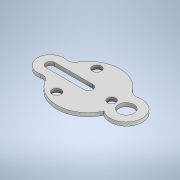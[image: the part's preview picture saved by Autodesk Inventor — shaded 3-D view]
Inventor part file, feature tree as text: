
AUTODESK INVENTOR PART (.ipt)
format: ipt  version: 2021 (Build 250183000, 183)  size: 151,040 bytes
history: native  units: mm
features: extrude x1, sketch x1
ambient origin geometry x8: Origin, YZ Plane, XZ Plane, XY Plane, X Axis, Y Axis, Z Axis, Center Point
bodies: Solid1 (feature_tree)
feature tree (2):
  extrude  "Extrusion1"  Depth=106.0mm
  sketch  "Sketch1"  dims[d1=72.0mm d2=106.0mm d3=40.0mm d4=0.0mm d5=40.0mm d7=90.0mm d8=212.0mm d9=50.0mm d10=50.0mm d11=0.0mm d12=130.0mm d13=23.0mm d14=43.0mm d15=25.0mm d16=25.0mm d18=120.0deg d19=120.0deg d20=25.0mm d21=25.0mm d22=10.0mm d23=0.0mm]
